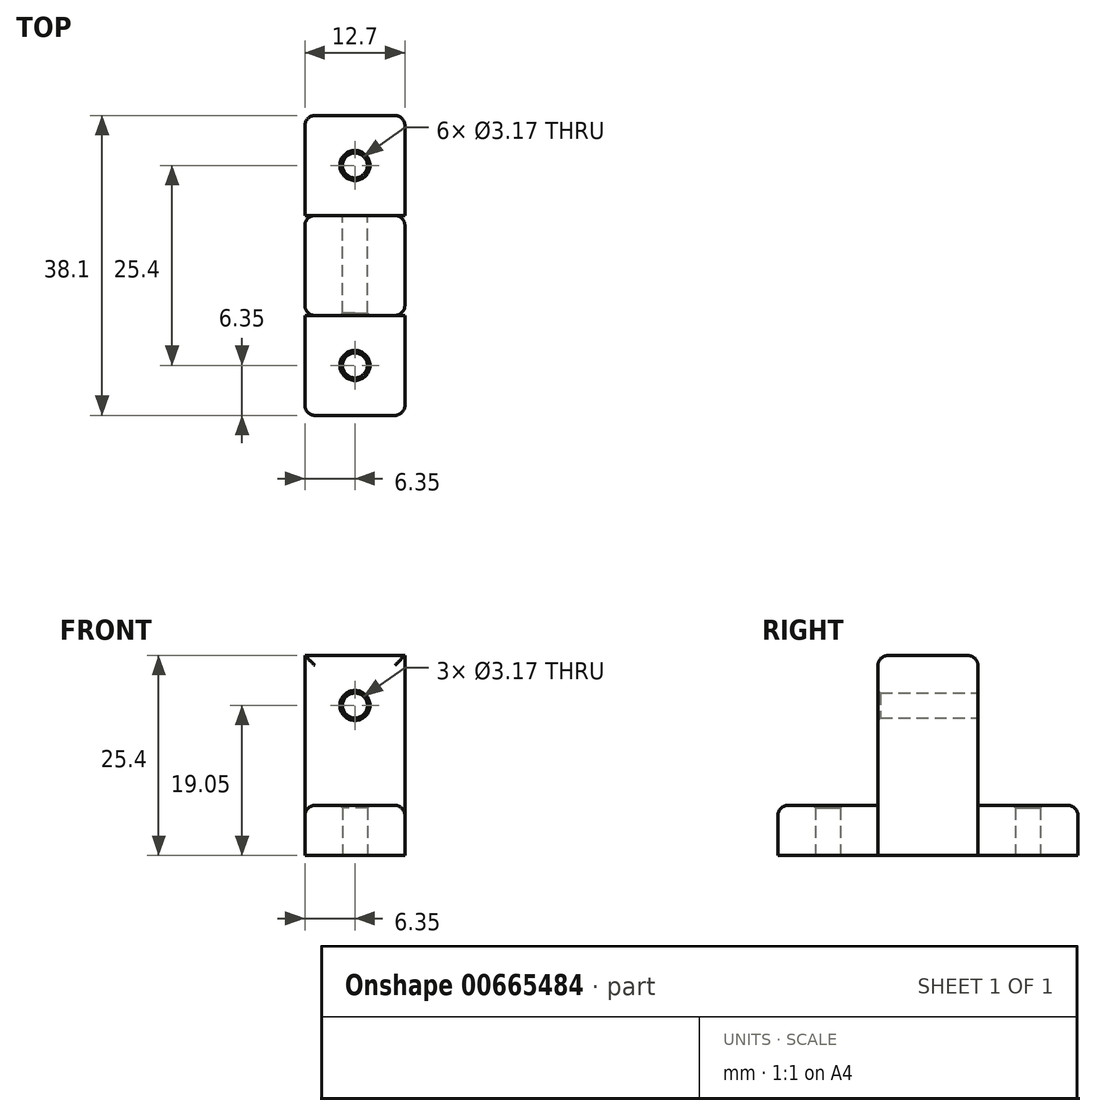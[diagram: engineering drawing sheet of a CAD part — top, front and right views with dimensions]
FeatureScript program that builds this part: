
annotation { "Feature Type Name" : "Feature", "Feature Type Description" : "" }
export const myFeature = defineFeature(function(context is Context, id is Id, definition is map)
    precondition{}
    {
        {
            var Q0;
            Q0=qCreatedBy(makeId("Top.planeOp"),FACE);
            var sketch = newSketch(context, id + "F0", { "sketchPlane" : qUnion([Q0])});
            skLineSegment(sketch, "E0.bottom", {"start": v(-6.35, 19.05) * mm, "end": v(6.35, 19.05) * mm});
            skLineSegment(sketch, "E0.top", {"start": v(-6.35, -19.05) * mm, "end": v(6.35, -19.05) * mm});
            skLineSegment(sketch, "E0.left", {"start": v(-6.35, 19.05) * mm, "end": v(-6.35, -19.05) * mm});
            skLineSegment(sketch, "E0.right", {"start": v(6.35, 19.05) * mm, "end": v(6.35, -19.05) * mm});
            skPoint(sketch, "E0.middle", {"position": v(0, 0) * mm});
            skCircle(sketch, "E1", {"center": v(0, 12.7) * mm, "radius": 1.59 * mm});
            skCircle(sketch, "E2", {"center": v(0, -12.7) * mm, "radius": 1.59 * mm});
            skLineSegment(sketch, "E3.bottom", {"start": v(6.35, 6.35) * mm, "end": v(-6.35, 6.35) * mm});
            skLineSegment(sketch, "E3.top", {"start": v(6.35, -6.35) * mm, "end": v(-6.35, -6.35) * mm});
            skLineSegment(sketch, "E3.left", {"start": v(6.35, 6.35) * mm, "end": v(6.35, -6.35) * mm});
            skLineSegment(sketch, "E3.right", {"start": v(-6.35, 6.35) * mm, "end": v(-6.35, -6.35) * mm});
            skSolve(sketch);
        }
        {
            var Q0;
            {var subQ1=sQuery(id+"F0.wireOp",EDGE,"E0.bottom");Q0=makeQuery(id+"F0.imprint","IMPRINT",FACE,{"disambiguationData":[TD([[makeQuery(id+"F0.imprint","IMPRINT",EDGE,{"derivedFrom":subQ1}),-1.0]])]});}
            var Q1;
            {var subQ1=sQuery(id+"F0.wireOp",EDGE,"E0.top");Q1=makeQuery(id+"F0.imprint","IMPRINT",FACE,{"disambiguationData":[TD([[makeQuery(id+"F0.imprint","IMPRINT",EDGE,{"derivedFrom":subQ1}),1.0]])]});}
            extrude(context, id + "F1", {"entities" : qUnion([Q0, Q1]), "depth" : 6.35 * mm, "offsetDistance" : 25.4 * mm});
        }
        {
            var Q0;
            Q0=makeQuery(id+"F0.imprint","IMPRINT",FACE,{"disambiguationData":[TD([[makeQuery(id+"F0.imprint","IMPRINT",EDGE,{"derivedFrom":sQuery(id+"F0.wireOp",EDGE,"E3.bottom")}),1.0]])]});
            extrude(context, id + "F2", {"entities" : qUnion([Q0]), "depth" : 25.4 * mm, "offsetDistance" : 25.4 * mm});
        }
        {
            var Q0;
            Q0=makeQuery(id+"F2.opExtrude","SWEPT_FACE",FACE,{"disambiguationData":[OSD([sQuery(id+"F0.wireOp",EDGE,"E3.bottom")])]});
            var sketch = newSketch(context, id + "F3", { "sketchPlane" : qUnion([Q0])});
            skCircle(sketch, "E4", {"center": v(0, 19.05) * mm, "radius": 1.59 * mm});
            skSolve(sketch);
        }
        {
            var Q0;
            Q0=makeQuery(id+"F3.imprint","IMPRINT",FACE,{"disambiguationData":[TD([[makeQuery(id+"F3.imprint","IMPRINT",EDGE,{"derivedFrom":sQuery(id+"F3.wireOp",EDGE,"E4")}),1.0]])]});
            extrude(context, id + "F4", {"entities" : qUnion([Q0]), "operationType" : NewBodyOperationType.REMOVE, "oppositeDirection" : true, "depth" : 25.4 * mm, "offsetDistance" : 25.4 * mm});
        }
        {
            var Q0;
            Q0=makeQuery(id+"F2.opExtrude","CAP_EDGE",EDGE,{"disambiguationData":[OSD([sQuery(id+"F0.wireOp",EDGE,"E3.bottom")])],"isStart":false});
            var Q1;
            Q1=makeQuery(id+"F2.opExtrude","CAP_EDGE",EDGE,{"disambiguationData":[OSD([sQuery(id+"F0.wireOp",EDGE,"E3.left")])],"isStart":false});
            var Q2;
            Q2=makeQuery(id+"F2.opExtrude","CAP_EDGE",EDGE,{"disambiguationData":[OSD([sQuery(id+"F0.wireOp",EDGE,"E3.top")])],"isStart":false});
            var Q3;
            Q3=makeQuery(id+"F2.opExtrude","CAP_EDGE",EDGE,{"disambiguationData":[OSD([sQuery(id+"F0.wireOp",EDGE,"E3.right")])],"isStart":false});
            var Q4;
            Q4=makeQuery(id+"F2.opExtrude","SWEPT_EDGE",EDGE,{"disambiguationData":[OSD([sQuery(id+"F0.wireOp",EDGE,"E0.right"),sQuery(id+"F0.wireOp",EDGE,"E3.bottom"),sQuery(id+"F0.wireOp",EDGE,"E3.left")])]});
            var Q5;
            Q5=makeQuery(id+"F2.opExtrude","SWEPT_EDGE",EDGE,{"disambiguationData":[OSD([sQuery(id+"F0.wireOp",EDGE,"E0.right"),sQuery(id+"F0.wireOp",EDGE,"E3.top"),sQuery(id+"F0.wireOp",EDGE,"E3.left")])]});
            var Q6;
            {var subQ0=sQuery(id+"F0.wireOp",EDGE,"E0.right");Q6=makeQuery(id+"F1.opExtrude","CAP_EDGE",EDGE,{"disambiguationData":[OSD([subQ0]),TDD([makeQuery(id+"F0.imprint","IMPRINT",EDGE,{"disambiguationData":[TD([[makeQuery(id+"F0.imprint","INTERSECT",VERTEX,{"derivedFrom":[sQuery(id+"F0.wireOp",EDGE,"E0.top"),subQ0]}),1.0]])],"derivedFrom":subQ0})])],"isStart":false});}
            var Q7;
            {var subQ0=sQuery(id+"F0.wireOp",EDGE,"E0.right");Q7=makeQuery(id+"F1.opExtrude","CAP_EDGE",EDGE,{"disambiguationData":[OSD([subQ0]),TDD([makeQuery(id+"F0.imprint","IMPRINT",EDGE,{"disambiguationData":[TD([[makeQuery(id+"F0.imprint","INTERSECT",VERTEX,{"derivedFrom":[sQuery(id+"F0.wireOp",EDGE,"E0.bottom"),subQ0]}),-1.0]])],"derivedFrom":subQ0})])],"isStart":false});}
            var Q8;
            Q8=makeQuery(id+"F2.opExtrude","SWEPT_EDGE",EDGE,{"disambiguationData":[OSD([sQuery(id+"F0.wireOp",EDGE,"E0.left"),sQuery(id+"F0.wireOp",EDGE,"E3.bottom"),sQuery(id+"F0.wireOp",EDGE,"E3.right")])]});
            var Q9;
            {var subQ0=sQuery(id+"F0.wireOp",EDGE,"E0.left");Q9=makeQuery(id+"F1.opExtrude","CAP_EDGE",EDGE,{"disambiguationData":[OSD([subQ0]),TDD([makeQuery(id+"F0.imprint","IMPRINT",EDGE,{"disambiguationData":[TD([[makeQuery(id+"F0.imprint","INTERSECT",VERTEX,{"derivedFrom":[sQuery(id+"F0.wireOp",EDGE,"E0.bottom"),subQ0]}),-1.0]])],"derivedFrom":subQ0})])],"isStart":false});}
            var Q10;
            Q10=makeQuery(id+"F2.opExtrude","SWEPT_EDGE",EDGE,{"disambiguationData":[OSD([sQuery(id+"F0.wireOp",EDGE,"E0.left"),sQuery(id+"F0.wireOp",EDGE,"E3.top"),sQuery(id+"F0.wireOp",EDGE,"E3.right")])]});
            var Q11;
            {var subQ0=sQuery(id+"F0.wireOp",EDGE,"E0.left");Q11=makeQuery(id+"F1.opExtrude","CAP_EDGE",EDGE,{"disambiguationData":[OSD([subQ0]),TDD([makeQuery(id+"F0.imprint","IMPRINT",EDGE,{"disambiguationData":[TD([[makeQuery(id+"F0.imprint","INTERSECT",VERTEX,{"derivedFrom":[sQuery(id+"F0.wireOp",EDGE,"E0.top"),subQ0]}),1.0]])],"derivedFrom":subQ0})])],"isStart":false});}
            var Q12;
            Q12=makeQuery(id+"F1.opExtrude","CAP_EDGE",EDGE,{"disambiguationData":[OSD([sQuery(id+"F0.wireOp",EDGE,"E0.top")])],"isStart":false});
            var Q13;
            Q13=makeQuery(id+"F1.opExtrude","SWEPT_EDGE",EDGE,{"disambiguationData":[OSD([sQuery(id+"F0.wireOp",EDGE,"E0.top"),sQuery(id+"F0.wireOp",EDGE,"E0.left")])]});
            var Q14;
            Q14=makeQuery(id+"F1.opExtrude","SWEPT_EDGE",EDGE,{"disambiguationData":[OSD([sQuery(id+"F0.wireOp",EDGE,"E0.top"),sQuery(id+"F0.wireOp",EDGE,"E0.right")])]});
            var Q15;
            Q15=makeQuery(id+"F1.opExtrude","SWEPT_EDGE",EDGE,{"disambiguationData":[OSD([sQuery(id+"F0.wireOp",EDGE,"E0.bottom"),sQuery(id+"F0.wireOp",EDGE,"E0.right")])]});
            var Q16;
            Q16=makeQuery(id+"F1.opExtrude","SWEPT_EDGE",EDGE,{"disambiguationData":[OSD([sQuery(id+"F0.wireOp",EDGE,"E0.bottom"),sQuery(id+"F0.wireOp",EDGE,"E0.left")])]});
            var Q17;
            Q17=makeQuery(id+"F1.opExtrude","CAP_EDGE",EDGE,{"disambiguationData":[OSD([sQuery(id+"F0.wireOp",EDGE,"E0.bottom")])],"isStart":false});
            fillet(context, id + "F5", {"entities" : qUnion([Q0, Q1, Q2, Q3, Q4, Q5, Q6, Q7, Q8, Q9, Q10, Q11, Q12, Q13, Q14, Q15, Q16, Q17]), "radius" : 1.27 * mm, "tangentPropagation" : true, "allowEdgeOverflow" : false});
        }
        {
            var Q0;
            Q0=makeQuery(id+"F1.opExtrude","CAP_EDGE",EDGE,{"disambiguationData":[OSD([sQuery(id+"F0.wireOp",EDGE,"E2")])],"isStart":false});
            var Q1;
            Q1=makeQuery(id+"F1.opExtrude","CAP_EDGE",EDGE,{"disambiguationData":[OSD([sQuery(id+"F0.wireOp",EDGE,"E1")])],"isStart":false});
            var Q2;
            Q2=makeQuery(id+"F4.boolean.opBoolean","COPY",EDGE,{"derivedFrom":makeQuery(id+"F4.opExtrude","CAP_EDGE",EDGE,{"disambiguationData":[OSD([sQuery(id+"F3.wireOp",EDGE,"E4")])],"isStart":true})});
            var Q3;
            Q3=makeQuery(id+"F4.boolean.opBoolean","INTERSECT",EDGE,{"derivedFrom":[makeQuery(id+"F2.opExtrude","SWEPT_FACE",FACE,{"disambiguationData":[OSD([sQuery(id+"F0.wireOp",EDGE,"E3.top")])]}),makeQuery(id+"F4.opExtrude","SWEPT_FACE",FACE,{"disambiguationData":[OSD([sQuery(id+"F3.wireOp",EDGE,"E4")])]})]});
            chamfer(context, id + "F6", {"entities" : qUnion([Q0, Q1, Q2, Q3]), "width" : 0.32 * mm, "tangentPropagation" : true});
        }
    });
